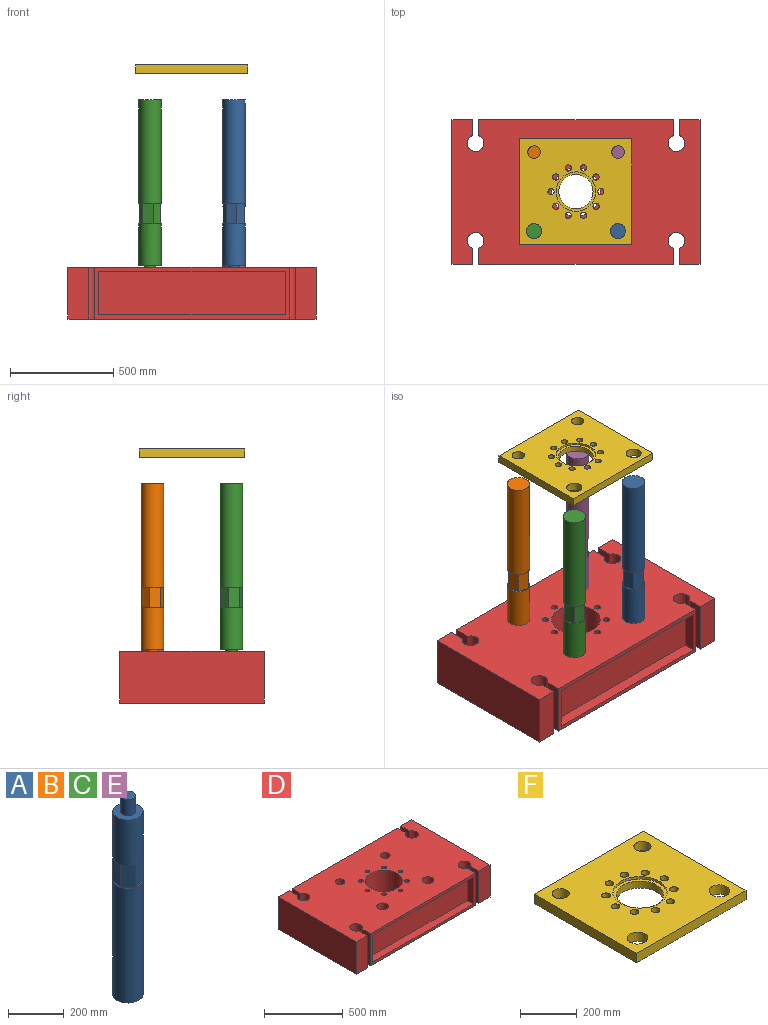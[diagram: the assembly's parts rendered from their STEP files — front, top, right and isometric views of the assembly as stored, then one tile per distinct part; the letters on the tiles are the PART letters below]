
ASSEMBLY  parts=6 mates=5
PART A: 25 faces, bbox 108.5x108.5x870 mm
  f0: plane 0.07x0.03mm, normal (0,0,1), area 0mm2, adj f8,f13,f20
  f1: plane 0.07x0.03mm, normal (0,0,1), area 0mm2, adj f8,f9,f20
  f2: plane 0.06x0.05mm, normal (0,0,1), area 0mm2, adj f9,f10,f20
  f3: plane 0.07x0.03mm, normal (0,0,1), area 0mm2, adj f10,f11,f20
  f4: plane 0.07x0.03mm, normal (0,0,1), area 0mm2, adj f11,f12,f20
  f5: plane 108.49x108.49mm, normal (0,0,1), area 1639.1mm2, adj f6,f8,f9,f10,f11,f12,f13
  f6: cylinder r=54.24mm len=500mm, axis (0,0,-1), area 170413.7mm2, adj f5,f7
  f7: plane 108.49x108.49mm, normal (0,0,-1), area 9244mm2, adj f6
  f8: plane 100x38.61mm, normal (0.71,0.7,0), area 5410.3mm2, adj f0,f1,f5,f9,f13,f15
  f9: plane 100x52.39mm, normal (-0.25,0.97,0), area 5410.3mm2, adj f1,f2,f5,f8,f10,f16
  f10: plane 100x52.13mm, normal (-0.96,0.27,0), area 5410.3mm2, adj f2,f3,f5,f9,f11,f17
  f11: plane 100x38.61mm, normal (-0.71,-0.7,0), area 5410.3mm2, adj f3,f4,f5,f10,f12,f18
  f12: plane 100x52.39mm, normal (0.25,-0.97,0), area 5410.3mm2, adj f4,f5,f11,f13,f14,f19
  f13: plane 100x52.13mm, normal (0.96,-0.27,0), area 5410.3mm2, adj f0,f5,f8,f12,f14,f22
  f14: plane 0.06x0.05mm, normal (0,0,1), area 0mm2, adj f12,f13,f20
  f15: plane 38.55x37.84mm, normal (0,0,-1), area 263.9mm2, adj f8,f20
  f16: plane 52.3x15.46mm, normal (0,0,-1), area 263.9mm2, adj f9,f20
  f17: plane 52.04x16.17mm, normal (0,0,-1), area 263.9mm2, adj f10,f20
  f18: plane 38.55x37.84mm, normal (0,0,-1), area 263.9mm2, adj f11,f20
  f19: plane 52.3x15.46mm, normal (0,0,-1), area 263.9mm2, adj f12,f20
  f20: cylinder r=54.08mm len=200mm, axis (0,0,-1), area 67959.6mm2, adj f0,f1,f2,f3,f4,f14,f15,f16
  f21: plane 108.16x108.16mm, normal (0,0,1), area 6909.1mm2, adj f20,f23
  f22: plane 52.04x16.17mm, normal (0,0,-1), area 263.9mm2, adj f13,f20
  f23: cylinder r=26.93mm len=70mm, axis (0,0,-1), area 11846.5mm2, adj f21,f24
  f24: plane 53.87x53.87mm, normal (0,0,1), area 2279.2mm2, adj f23
PART B: same geometry as A
PART C: same geometry as A
PART D: 49 faces, bbox 1200x700x250 mm
  f0: plane 941.92x250mm, normal (0,-1,0), area 46076.9mm2, adj f2,f15,f16,f30,f44,f45,f46,f47
  f1: plane 941.92x250mm, normal (0,1,0), area 50276.9mm2, adj f2,f6,f7,f30,f39,f40,f41,f42
  f2: plane 1200x700mm, normal (0,0,1), area 747628.4mm2, adj f0,f1,f3,f4,f5,f6,f7,f8
  f3: plane 250x99.04mm, normal (0,1,0), area 24759.6mm2, adj f2,f4,f28,f30
  f4: plane 250x76.93mm, normal (-1,0,0), area 19231.8mm2, adj f2,f3,f5,f30
  f5: cylinder r=40mm len=250mm, axis (0,0,-1), area 55143.9mm2, adj f2,f4,f6,f30
  f6: plane 250x76.93mm, normal (1,0,0), area 19231.8mm2, adj f1,f2,f5,f30
  f7: plane 250x76.93mm, normal (-1,0,0), area 19231.8mm2, adj f1,f2,f8,f30
  f8: cylinder r=40mm len=250mm, axis (0,0,-1), area 55143.9mm2, adj f2,f7,f9,f30
  f9: plane 250x76.93mm, normal (1,0,0), area 19231.8mm2, adj f2,f8,f10,f30
  f10: plane 250x99.04mm, normal (0,1,0), area 24759.6mm2, adj f2,f9,f11,f30
  f11: plane 700x250mm, normal (-1,0,0), area 175000mm2, adj f2,f10,f12,f30
  f12: plane 250x99.04mm, normal (0,-1,0), area 24759.6mm2, adj f2,f11,f13,f30
  f13: plane 250x76.93mm, normal (1,0,0), area 19231.8mm2, adj f2,f12,f14,f30
  f14: cylinder r=40mm len=250mm, axis (0,0,-1), area 55143.9mm2, adj f2,f13,f15,f30
  f15: plane 250x76.93mm, normal (-1,0,0), area 19231.8mm2, adj f0,f2,f14,f30
  f16: plane 250x76.93mm, normal (1,0,0), area 19231.8mm2, adj f0,f2,f17,f30
  f17: cylinder r=40mm len=250mm, axis (0,0,-1), area 55143.9mm2, adj f2,f16,f18,f30
  f18: plane 250x76.93mm, normal (-1,0,0), area 19231.8mm2, adj f2,f17,f19,f30
  f19: plane 250x99.04mm, normal (0,-1,0), area 24759.6mm2, adj f2,f18,f28,f30
  f20: cylinder r=15mm len=250mm, axis (0,0,-1), area 23561.9mm2, adj f2,f30
  f21: cylinder r=15mm len=250mm, axis (0,0,-1), area 23561.9mm2, adj f2,f30
  f22: cylinder r=15mm len=250mm, axis (0,0,-1), area 23561.9mm2, adj f2,f30
  f23: cylinder r=15mm len=250mm, axis (0,0,-1), area 23561.9mm2, adj f2,f30
  f24: cylinder r=15mm len=250mm, axis (0,0,-1), area 23561.9mm2, adj f2,f30
  f25: cylinder r=15mm len=250mm, axis (0,0,-1), area 23561.9mm2, adj f2,f30
  f26: cylinder r=15mm len=250mm, axis (0,0,-1), area 23561.9mm2, adj f2,f30
  f27: cylinder r=117.74mm len=250mm, axis (0,0,-1), area 184945.9mm2, adj f2,f30
  f28: plane 700x250mm, normal (1,0,0), area 175000mm2, adj f2,f3,f19,f30
  f29: cylinder r=15mm len=250mm, axis (0,0,-1), area 23561.9mm2, adj f2,f30
  f30: plane 1200x700mm, normal (0,0,-1), area 761691.8mm2, adj f0,f1,f3,f4,f5,f6,f7,f8
  f31: cylinder r=30.22mm len=60.44mm, axis (0,0,1), area 11393.5mm2, adj f2,f32
  f32: plane 60.44x60.44mm, normal (0,0,1), area 2869.5mm2, adj f31
  f33: cylinder r=36.4mm len=72.8mm, axis (0,0,1), area 13722mm2, adj f2,f34
  f34: plane 72.8x72.8mm, normal (0,0,1), area 4162.2mm2, adj f33
  f35: cylinder r=36.4mm len=72.8mm, axis (0,0,1), area 13722mm2, adj f2,f36
  f36: plane 72.8x72.8mm, normal (0,0,1), area 4162.2mm2, adj f35
  f37: cylinder r=30.22mm len=60.44mm, axis (0,0,1), area 11393.5mm2, adj f2,f38
  f38: plane 60.44x60.44mm, normal (0,0,1), area 2869.5mm2, adj f37
  f39: plane 881.92x55mm, normal (0,0,1), area 48505.8mm2, adj f1,f40,f42,f43
  f40: plane 210x55mm, normal (1,0,0), area 11550mm2, adj f1,f39,f41,f43
  f41: plane 881.92x55mm, normal (0,0,-1), area 48505.8mm2, adj f1,f40,f42,f43
  f42: plane 210x55mm, normal (-1,0,0), area 11550mm2, adj f1,f39,f41,f43
  f43: plane 881.92x210mm, normal (0,1,0), area 185203.9mm2, adj f39,f40,f41,f42
  f44: plane 901.92x55mm, normal (0,0,-1), area 49605.8mm2, adj f0,f45,f47,f48
  f45: plane 210x55mm, normal (1,0,0), area 11550mm2, adj f0,f44,f46,f48
  f46: plane 901.92x55mm, normal (0,0,1), area 49605.8mm2, adj f0,f45,f47,f48
  f47: plane 210x55mm, normal (-1,0,0), area 11550mm2, adj f0,f44,f46,f48
  f48: plane 901.92x210mm, normal (0,-1,0), area 189403.9mm2, adj f44,f45,f46,f47
PART E: same geometry as A
PART F: 23 faces, bbox 542.2x511.2x40 mm
  f0: cylinder r=82.99mm len=165.98mm, axis (0,0,-1), area 15643.4mm2, adj f20,f22
  f1: plane 542.25x40mm, normal (0,1,0), area 21689.8mm2, adj f2,f18,f19,f20
  f2: plane 511.2x40mm, normal (-1,0,0), area 20447.8mm2, adj f1,f3,f19,f20
  f3: plane 542.25x40mm, normal (0,-1,0), area 21689.8mm2, adj f2,f18,f19,f20
  f4: cylinder r=30.22mm len=60.44mm, axis (0,0,-1), area 7595.7mm2, adj f19,f20
  f5: cylinder r=36.4mm len=72.8mm, axis (0,0,-1), area 9148mm2, adj f19,f20
  f6: cylinder r=36.4mm len=72.8mm, axis (0,0,-1), area 9148mm2, adj f19,f20
  f7: cylinder r=15mm len=40mm, axis (0,0,-1), area 3769.9mm2, adj f19,f20
  f8: cylinder r=15mm len=40mm, axis (0,0,-1), area 3769.9mm2, adj f19,f20
  f9: cylinder r=15mm len=40mm, axis (0,0,-1), area 3769.9mm2, adj f19,f20
  f10: cylinder r=15mm len=40mm, axis (0,0,-1), area 3769.9mm2, adj f19,f20
  f11: cylinder r=15mm len=40mm, axis (0,0,-1), area 3769.9mm2, adj f19,f20
  f12: cylinder r=15mm len=40mm, axis (0,0,-1), area 3769.9mm2, adj f19,f20
  f13: cylinder r=15mm len=40mm, axis (0,0,-1), area 3769.9mm2, adj f19,f20
  f14: cylinder r=15mm len=40mm, axis (0,0,-1), area 3769.9mm2, adj f19,f20
  f15: cylinder r=15mm len=40mm, axis (0,0,-1), area 3769.9mm2, adj f19,f20
  f16: cylinder r=15mm len=40mm, axis (0,0,-1), area 3769.9mm2, adj f19,f20
  f17: cylinder r=30.22mm len=60.44mm, axis (0,0,-1), area 7595.7mm2, adj f19,f20
  f18: plane 511.2x40mm, normal (1,0,0), area 20447.8mm2, adj f1,f3,f19,f20
  f19: plane 542.25x511.2mm, normal (0,0,1), area 227343.7mm2, adj f1,f2,f3,f4,f5,f6,f7,f8
  f20: plane 542.25x511.2mm, normal (0,0,-1), area 234423.6mm2, adj f0,f1,f2,f3,f4,f5,f6,f7
  f21: cylinder r=95.61mm len=191.22mm, axis (0,0,1), area 6007.3mm2, adj f19,f22
  f22: plane 191.22x191.22mm, normal (0,0,1), area 7079.9mm2, adj f0,f21
PLACE A rot(axis=(0,1,0),180deg) t=(203.07,-191.2,1060)mm
PLACE B rot(axis=(0,1,0),180deg) t=(-203.07,191.2,1060)mm
PLACE C rot(axis=(0,1,0),180deg) t=(-203.07,-191.2,1060)mm
PLACE D at identity fixed
PLACE E rot(axis=(1,0,0),180deg) t=(203.07,191.2,1043.57)mm
PLACE F rot(axis=(0,1,0),0deg) t=(-0.5,-0.33,1189.45)mm
MATE fastened B.f23 <-> D.f31  axis (0,0,-1) through (-203.07,191.2,190)mm
MATE slider F.f4 <-> B.f6  axis (0,0,-1) through (-203.07,191.2,1189.45)mm
MATE fastened C.f23 <-> D.f33  axis (0,0,-1) through (-203.07,-191.2,190)mm
MATE slider E.f23 <-> D.f37  axis (0,0,-1) through (203.07,191.2,173.57)mm
MATE fastened A.f23 <-> D.f35  axis (0,0,-1) through (203.07,-191.2,190)mm
